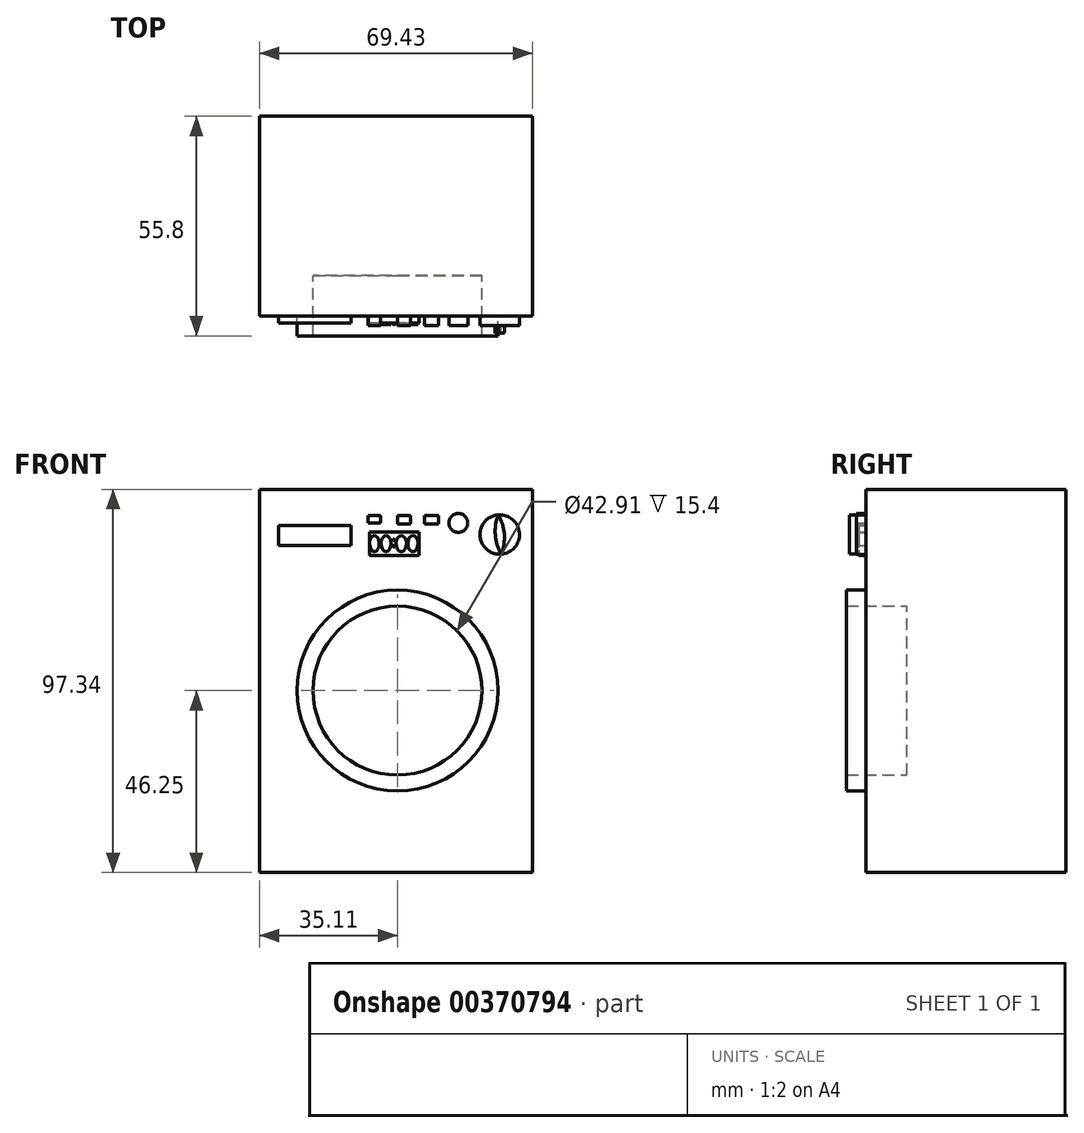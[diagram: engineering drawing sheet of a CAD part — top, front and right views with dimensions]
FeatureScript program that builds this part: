
annotation { "Feature Type Name" : "Feature", "Feature Type Description" : "" }
export const myFeature = defineFeature(function(context is Context, id is Id, definition is map)
    precondition{}
    {
        {
            var Q0;
            Q0=qCreatedBy(makeId("Front.planeOp"),FACE);
            var sketch = newSketch(context, id + "F0", { "sketchPlane" : qUnion([Q0])});
            skLineSegment(sketch, "E0.bottom", {"start": v(-35.1, 51.1) * mm, "end": v(34.32, 51.1) * mm});
            skLineSegment(sketch, "E0.top", {"start": v(-35.1, -46.25) * mm, "end": v(34.32, -46.25) * mm});
            skLineSegment(sketch, "E0.left", {"start": v(-35.1, 51.1) * mm, "end": v(-35.1, -46.25) * mm});
            skLineSegment(sketch, "E0.right", {"start": v(34.32, 51.1) * mm, "end": v(34.32, -46.25) * mm});
            skSolve(sketch);
        }
        {
            var Q0;
            Q0=makeQuery(id+"F0.imprint","IMPRINT",FACE,{"disambiguationData":[TD([[makeQuery(id+"F0.imprint","IMPRINT",EDGE,{"derivedFrom":sQuery(id+"F0.wireOp",EDGE,"E0.bottom")}),-1.0]])]});
            extrude(context, id + "F1", {"entities" : qUnion([Q0]), "depth" : 50.8 * mm});
        }
        {
            var Q0;
            Q0=makeQuery(id+"F1.opExtrude","CAP_FACE",FACE,{"disambiguationData":[OSD([sQuery(id+"F0.wireOp",EDGE,"E0.bottom"),sQuery(id+"F0.wireOp",EDGE,"E0.top"),sQuery(id+"F0.wireOp",EDGE,"E0.left"),sQuery(id+"F0.wireOp",EDGE,"E0.right")])],"isStart":false});
            var sketch = newSketch(context, id + "F2", { "sketchPlane" : qUnion([Q0])});
            skLineSegment(sketch, "E1.bottom", {"start": v(-30.23, 41.98) * mm, "end": v(-11.86, 41.98) * mm});
            skLineSegment(sketch, "E1.top", {"start": v(-30.23, 36.85) * mm, "end": v(-11.86, 36.85) * mm});
            skLineSegment(sketch, "E1.left", {"start": v(-30.23, 41.98) * mm, "end": v(-30.23, 36.85) * mm});
            skLineSegment(sketch, "E1.right", {"start": v(-11.86, 41.98) * mm, "end": v(-11.86, 36.85) * mm});
            skLineSegment(sketch, "E2.bottom", {"start": v(-7.16, 40.27) * mm, "end": v(5.45, 40.27) * mm});
            skLineSegment(sketch, "E2.top", {"start": v(-7.16, 34.3) * mm, "end": v(5.45, 34.3) * mm});
            skLineSegment(sketch, "E2.left", {"start": v(-7.16, 40.27) * mm, "end": v(-7.16, 34.3) * mm});
            skLineSegment(sketch, "E2.right", {"start": v(5.45, 40.27) * mm, "end": v(5.45, 34.3) * mm});
            skSolve(sketch);
        }
        {
            var Q0;
            Q0 = qSketchRegion(id + "F2", true);
            extrude(context, id + "F3", {"entities" : qUnion([Q0]), "operationType" : NewBodyOperationType.ADD, "depth" : 1.78 * mm});
        }
        {
            var Q0;
            Q0=makeQuery(id+"F1.opExtrude","CAP_FACE",FACE,{"disambiguationData":[OSD([sQuery(id+"F0.wireOp",EDGE,"E0.bottom"),sQuery(id+"F0.wireOp",EDGE,"E0.top"),sQuery(id+"F0.wireOp",EDGE,"E0.left"),sQuery(id+"F0.wireOp",EDGE,"E0.right")])],"isStart":false});
            var sketch = newSketch(context, id + "F4", { "sketchPlane" : qUnion([Q0])});
            skCircle(sketch, "E3", {"center": v(0, 0) * mm, "radius": 21.46 * mm});
            skCircle(sketch, "E4", {"center": v(0, 0) * mm, "radius": 25.51 * mm});
            skSolve(sketch);
        }
        {
            var Q0;
            Q0=makeQuery(id+"F4.imprint","IMPRINT",FACE,{"disambiguationData":[TD([[makeQuery(id+"F4.imprint","IMPRINT",EDGE,{"derivedFrom":sQuery(id+"F4.wireOp",EDGE,"E3")}),-1.0]])]});
            extrude(context, id + "F5", {"entities" : qUnion([Q0]), "operationType" : NewBodyOperationType.ADD, "depth" : 5 * mm});
        }
        {
            var Q0;
            {var subQ0=sQuery(id+"F0.wireOp",EDGE,"E0.left");var subQ1=sQuery(id+"F0.wireOp",EDGE,"E0.bottom");var subQ2=sQuery(id+"F0.wireOp",EDGE,"E0.right");var subQ3=sQuery(id+"F0.wireOp",EDGE,"E0.top");Q0=makeQuery(id+"F5.boolean.opBoolean","SPLIT",FACE,{"disambiguationData":[TD([makeQuery(id+"F1.opExtrude","SWEPT_FACE",FACE,{"disambiguationData":[OSD([subQ1])]})])],"derivedFrom":makeQuery(id+"F1.opExtrude","CAP_FACE",FACE,{"disambiguationData":[OSD([subQ1,subQ3,subQ0,subQ2])],"isStart":false})});}
            var sketch = newSketch(context, id + "F6", { "sketchPlane" : qUnion([Q0])});
            skLineSegment(sketch, "E5.bottom", {"start": v(-7.46, 44.47) * mm, "end": v(-4.31, 44.47) * mm});
            skLineSegment(sketch, "E5.top", {"start": v(-7.46, 42.58) * mm, "end": v(-4.31, 42.58) * mm});
            skLineSegment(sketch, "E5.left", {"start": v(-7.46, 44.47) * mm, "end": v(-7.46, 42.58) * mm});
            skLineSegment(sketch, "E5.right", {"start": v(-4.31, 44.47) * mm, "end": v(-4.31, 42.58) * mm});
            skLineSegment(sketch, "E6.bottom", {"start": v(0, 44.47) * mm, "end": v(3.26, 44.47) * mm});
            skLineSegment(sketch, "E6.top", {"start": v(0, 42.37) * mm, "end": v(3.26, 42.37) * mm});
            skLineSegment(sketch, "E6.left", {"start": v(0, 44.47) * mm, "end": v(0, 42.37) * mm});
            skLineSegment(sketch, "E6.right", {"start": v(3.26, 44.47) * mm, "end": v(3.26, 42.37) * mm});
            skLineSegment(sketch, "E7.bottom", {"start": v(6.83, 44.47) * mm, "end": v(10.4, 44.47) * mm});
            skLineSegment(sketch, "E7.top", {"start": v(6.83, 42.37) * mm, "end": v(10.4, 42.37) * mm});
            skLineSegment(sketch, "E7.left", {"start": v(6.83, 44.47) * mm, "end": v(6.83, 42.37) * mm});
            skLineSegment(sketch, "E7.right", {"start": v(10.4, 44.47) * mm, "end": v(10.4, 42.37) * mm});
            skCircle(sketch, "E8", {"center": v(15.46, 42.58) * mm, "radius": 2.4 * mm});
            skCircle(sketch, "E9", {"center": v(25.97, 39.64) * mm, "radius": 5.02 * mm});
            skSolve(sketch);
        }
        {
            var Q0;
            Q0 = qSketchRegion(id + "F6", true);
            extrude(context, id + "F7", {"entities" : qUnion([Q0]), "operationType" : NewBodyOperationType.ADD, "depth" : 2.4 * mm});
        }
        {
            var Q0;
            Q0=makeQuery(id+"F7.opExtrude","CAP_FACE",FACE,{"disambiguationData":[OSD([sQuery(id+"F6.wireOp",EDGE,"E9")])],"isStart":false});
            var sketch = newSketch(context, id + "F8", { "sketchPlane" : qUnion([Q0])});
            skArc(sketch, "E10", {"start": v(26.34, 34.64) * mm, "mid": v(27.14, 39.72) * mm, "end": v(25.63, 44.64) * mm});
            skArc(sketch, "E11", {"start": v(25.63, 44.64) * mm, "mid": v(24.84, 39.56) * mm, "end": v(26.34, 34.64) * mm});
            skSolve(sketch);
        }
        {
            var Q0;
            Q0 = qSketchRegion(id + "F8", true);
            extrude(context, id + "F9", {"entities" : qUnion([Q0]), "operationType" : NewBodyOperationType.ADD, "depth" : 1.8 * mm});
        }
        {
            var Q0;
            Q0=makeQuery(id+"F5.boolean.opBoolean","SPLIT",FACE,{"disambiguationData":[TD([makeQuery(id+"F5.opExtrude","SWEPT_FACE",FACE,{"disambiguationData":[OSD([sQuery(id+"F4.wireOp",EDGE,"E3")])]})])],"derivedFrom":makeQuery(id+"F1.opExtrude","CAP_FACE",FACE,{"disambiguationData":[OSD([sQuery(id+"F0.wireOp",EDGE,"E0.bottom"),sQuery(id+"F0.wireOp",EDGE,"E0.top"),sQuery(id+"F0.wireOp",EDGE,"E0.left"),sQuery(id+"F0.wireOp",EDGE,"E0.right")])],"isStart":false})});
            extrude(context, id + "F10", {"entities" : qUnion([Q0]), "operationType" : NewBodyOperationType.REMOVE, "oppositeDirection" : true, "depth" : 10.4 * mm});
        }
        {
            var Q0;
            Q0=makeQuery(id+"F3.opExtrude","CAP_FACE",FACE,{"disambiguationData":[OSD([sQuery(id+"F2.wireOp",EDGE,"E2.bottom"),sQuery(id+"F2.wireOp",EDGE,"E2.top"),sQuery(id+"F2.wireOp",EDGE,"E2.left"),sQuery(id+"F2.wireOp",EDGE,"E2.right")])],"isStart":false});
            var sketch = newSketch(context, id + "F11", { "sketchPlane" : qUnion([Q0])});
            skCircle(sketch, "E12", {"center": v(-0.97, 38.33) * mm, "radius": 0.18 * mm});
            skCircle(sketch, "E13", {"center": v(-0.94, 36.68) * mm, "radius": 0.2 * mm});
            skEllipse(sketch, "E14", {"center": v(-5.86, 37.35) * mm, "majorRadius": 2.01 * mm, "minorRadius": 1.22 * mm, "majorAxis": v(0, 1)});
            skEllipse(sketch, "E15", {"center": v(-2.9, 37.35) * mm, "majorRadius": 2.02 * mm, "minorRadius": 1.26 * mm, "majorAxis": v(0, 1)});
            skPoint(sketch, "E15.centerSnap0", {"position": v(-4.64, 37.35) * mm});
            skEllipse(sketch, "E16", {"center": v(0.95, 37.35) * mm, "majorRadius": 2.02 * mm, "minorRadius": 1.32 * mm, "majorAxis": v(0, 1)});
            skPoint(sketch, "E16.centerSnap0", {"position": v(-1.65, 37.35) * mm});
            skEllipse(sketch, "E17", {"center": v(3.91, 37.35) * mm, "majorRadius": 2.02 * mm, "minorRadius": 1.3 * mm, "majorAxis": v(0, 1)});
            skPoint(sketch, "E17.centerSnap0", {"position": v(2.27, 37.35) * mm});
            skSolve(sketch);
        }
        {
            var Q0;
            Q0 = qSketchRegion(id + "F11", true);
            extrude(context, id + "F12", {"entities" : qUnion([Q0]), "depth" : 0.32 * mm});
        }
    });
